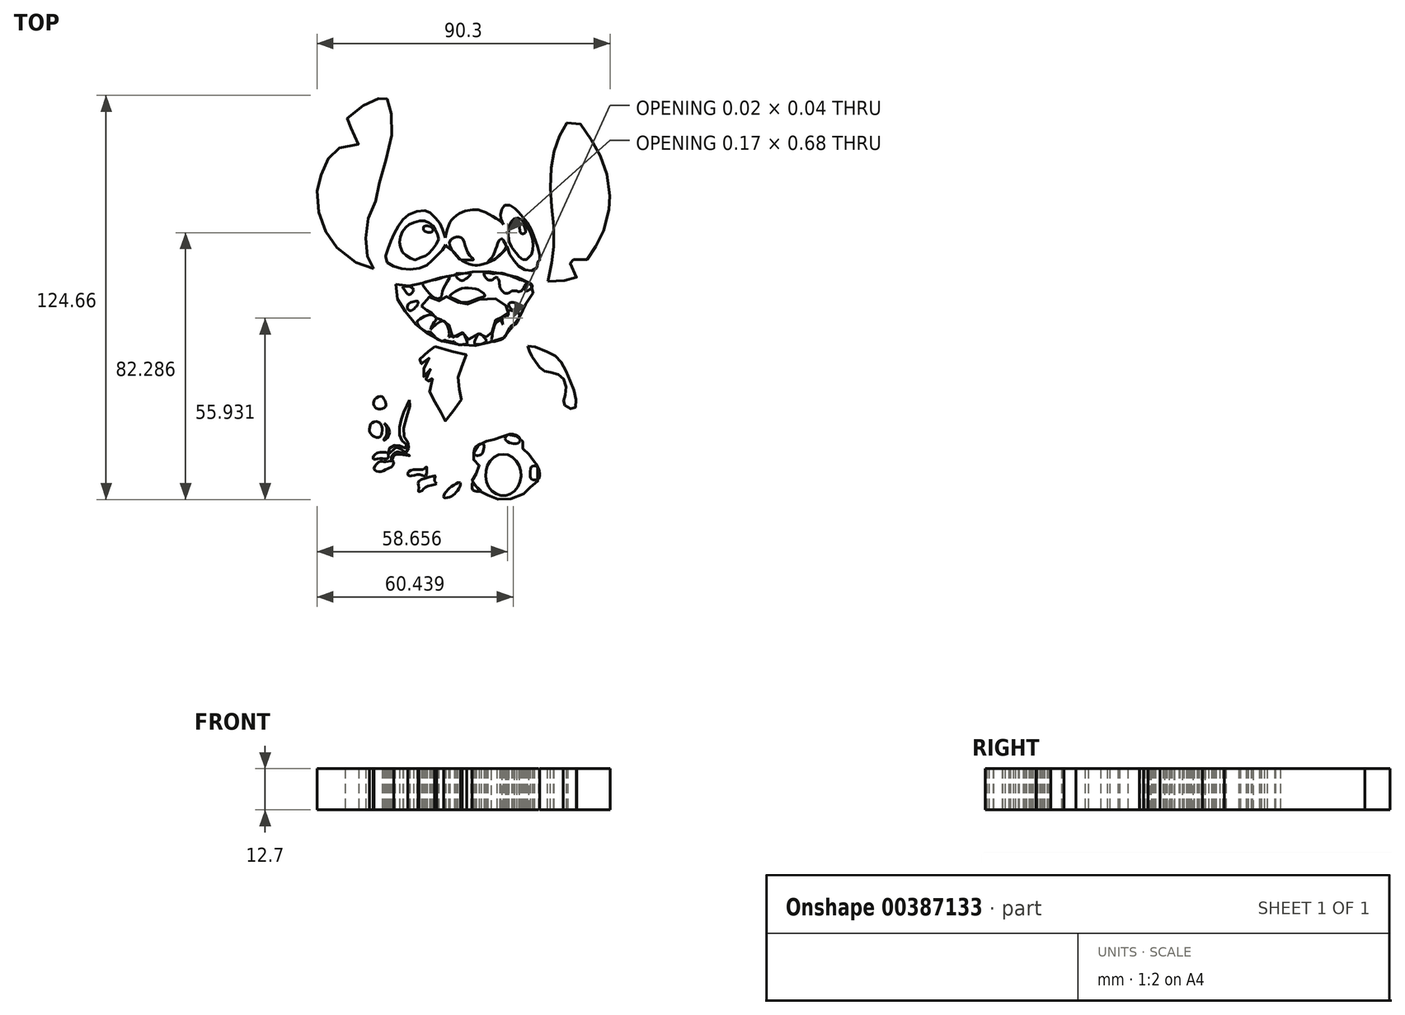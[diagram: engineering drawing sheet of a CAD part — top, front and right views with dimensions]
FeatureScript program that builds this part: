
annotation { "Feature Type Name" : "Feature", "Feature Type Description" : "" }
export const myFeature = defineFeature(function(context is Context, id is Id, definition is map)
    precondition{}
    {
        {
            var Q0;
            Q0=qCreatedBy(makeId("Top.planeOp"),FACE);
            var sketch = newSketch(context, id + "F0", { "sketchPlane" : qUnion([Q0])});
            skFitSpline(sketch, "E0", {"points": [v(-32.55, -2.75) * mm, v(-34, 0) * mm, v(-34.97, 5.48) * mm, v(-34.24, 12.5) * mm, v(-31.82, 18.3) * mm, v(-30.61, 24.6) * mm, v(-27.47, 35.25) * mm, v(-26.98, 44.45) * mm, v(-28.2, 49.04) * mm, v(-29.16, 50.74) * mm, v(-32.3, 49.04) * mm, v(-37.15, 46.87) * mm, v(-41.26, 42.27) * mm, v(-39.32, 40.57) * mm, v(-37.39, 35.5) * mm, v(-44.4, 34.28) * mm, v(-46.83, 30.4) * mm, v(-49, 25.57) * mm, v(-49.97, 20.49) * mm, v(-48.76, 12.02) * mm, v(-45.62, 5.97) * mm, v(-39.32, 0) * mm, v(-32.55, -2.75) * mm]});
            skFitSpline(sketch, "E1", {"points": [v(21.18, -6.62) * mm, v(22.63, 0) * mm, v(22.87, 4.51) * mm, v(22.87, 12.74) * mm, v(21.9, 18.8) * mm, v(22.15, 26.54) * mm, v(22.63, 32.35) * mm, v(24.33, 36.94) * mm, v(25.78, 41.06) * mm, v(29.4, 43) * mm, v(33.04, 39.36) * mm, v(36.43, 33.8) * mm, v(39.09, 27.5) * mm, v(40.3, 19.28) * mm, v(40.06, 16.13) * mm, v(37.88, 7.9) * mm, v(35.46, 3.55) * mm, v(33.04, 0) * mm, v(29.65, 0) * mm, v(27.23, 0) * mm, v(29.4, -2.75) * mm, v(29.65, -5.9) * mm, v(26.26, -6.38) * mm, v(21.18, -6.62) * mm]});
            skFitSpline(sketch, "E2", {"points": [v(-10.38, 4.73) * mm, v(-11.39, 9.62) * mm, v(-12.54, 11.78) * mm, v(-14.99, 14.51) * mm, v(-17.14, 15.23) * mm, v(-21.75, 13.94) * mm, v(-24.34, 11.35) * mm, v(-26.5, 7.46) * mm, v(-28.08, 3.43) * mm, v(-28.8, 0) * mm, v(-26.5, -1.9) * mm, v(-21.9, -2.9) * mm, v(-17.14, -2.18) * mm, v(-14.27, 0) * mm, v(-11.82, 2.57) * mm, v(-10.38, 4.73) * mm]});
            skFitSpline(sketch, "E3", {"points": [v(8.61, 4.15) * mm, v(10.49, 0) * mm, v(12.93, -2.47) * mm, v(16.24, -3.33) * mm, v(17.97, -1.75) * mm, v(18.26, 0) * mm, v(18.69, 0) * mm, v(18.26, 3.15) * mm, v(17.25, 6.02) * mm, v(16.39, 8.61) * mm, v(14.51, 11.92) * mm, v(12.36, 14.37) * mm, v(10.92, 15.95) * mm, v(8.9, 16.96) * mm, v(7.32, 16.39) * mm, v(6.6, 14.37) * mm, v(6.6, 13.22) * mm, v(7.46, 10.92) * mm, v(8.76, 8.04) * mm, v(8.61, 4.15) * mm]});
            skFitSpline(sketch, "E4", {"points": [v(0, 15.38) * mm, v(-2.6, 15.38) * mm, v(-4.77, 14.95) * mm, v(-7.93, 12.93) * mm, v(-9.66, 10.05) * mm, v(-10.38, 4.73) * mm, v(-8.08, 2.71) * mm, v(-5.63, 0) * mm, v(-1.75, -1.6) * mm, v(0, -1.6) * mm, v(4.44, 0) * mm, v(6.89, 2) * mm, v(8.61, 4.15) * mm, v(8.76, 8.04) * mm, v(7.46, 10.92) * mm, v(4.59, 13.22) * mm, v(0, 15.38) * mm]});
            skFitSpline(sketch, "E5", {"points": [v(-25.63, -7.5) * mm, v(-23.04, -7.8) * mm, v(-19.45, -7.8) * mm, v(-15.56, -6.5) * mm, v(-9.09, -4.91) * mm, v(-5.78, -4.34) * mm, v(0, -3.47) * mm, v(3.58, -3.62) * mm, v(6.6, -4.2) * mm, v(11.35, -5.2) * mm, v(15.1, -6.64) * mm, v(16.96, -8.8) * mm, v(16.53, -10.24) * mm, v(14.66, -12.97) * mm, v(13.08, -15.85) * mm, v(11.92, -18.73) * mm, v(9.9, -21.03) * mm, v(7.46, -24.05) * mm, v(3.87, -25.2) * mm, v(0, -26.35) * mm, v(-4.34, -26.21) * mm, v(-10.38, -25.5) * mm, v(-14.27, -23.48) * mm, v(-17.86, -21.6) * mm, v(-20.6, -18.58) * mm, v(-23.76, -14.7) * mm, v(-25.35, -11.53) * mm, v(-25.63, -7.5) * mm]});
            skSolve(sketch);
        }
        {
            var Q0;
            Q0=qCreatedBy(makeId("Top.planeOp"),FACE);
            var sketch = newSketch(context, id + "F1", { "sketchPlane" : qUnion([Q0])});
            skFitSpline(sketch, "E6", {"points": [v(-9.14, 5.43) * mm, v(-7.56, 7.02) * mm, v(-6.12, 7.02) * mm, v(-4.97, 6.3) * mm, v(-4.25, 4.14) * mm, v(-2.95, 1.4) * mm, v(-1.8, 0) * mm, v(-3.39, 0) * mm, v(-5.55, 0) * mm, v(-7.85, 2.27) * mm, v(-9.14, 5.43) * mm]});
            skFitSpline(sketch, "E7", {"points": [v(2.63, -0.7) * mm, v(3.84, 0.7) * mm, v(4.38, 1.6) * mm, v(4.74, 2.5) * mm, v(5.4, 4.14) * mm, v(6.2, 6.02) * mm, v(7.04, 6.5) * mm, v(7.4, 6.14) * mm, v(8, 4.99) * mm, v(8.31, 4.14) * mm, v(6.92, 2.2) * mm, v(5.35, 0.63) * mm, v(4.5, 0) * mm, v(2.63, -0.7) * mm]});
            skPoint(sketch, "E8.0.internal.orphan", {"position": v(-13.04, 5.43) * mm});
            skPoint(sketch, "E8.1.internal.orphan", {"position": v(-13.73, 4.14) * mm});
            skPoint(sketch, "E8.2.internal.orphan", {"position": v(-15.27, 2.27) * mm});
            skPoint(sketch, "E8.4.internal.orphan", {"position": v(-19.03, 0) * mm});
            skFitSpline(sketch, "E9", {"points": [v(-12.45, 6.44) * mm, v(-12.96, 8.15) * mm, v(-13.73, 9.7) * mm, v(-14.67, 10.9) * mm, v(-16.21, 11.83) * mm, v(-17.75, 12.09) * mm, v(-20.23, 11.49) * mm, v(-21.86, 10.72) * mm, v(-23.06, 9.6) * mm, v(-24.17, 7.81) * mm, v(-24.51, 5.5) * mm, v(-24.25, 4.13) * mm, v(-23.31, 2) * mm, v(-21.86, 1.05) * mm, v(-20.15, 0) * mm, v(-18.18, 0.7) * mm, v(-16.3, 1.4) * mm, v(-15.27, 2.27) * mm, v(-13.73, 4.14) * mm, v(-12.45, 6.44) * mm]});
            skFitSpline(sketch, "E10", {"points": [v(9.12, 9.35) * mm, v(9.54, 11.23) * mm, v(10.49, 12.52) * mm, v(11.77, 12.94) * mm, v(13.05, 12.35) * mm, v(14.08, 11.23) * mm, v(15.36, 9.35) * mm, v(16.05, 7.72) * mm, v(16.56, 4.14) * mm, v(16.05, 1.56) * mm, v(15.28, 0.8) * mm, v(14.34, 0) * mm, v(12.54, 0.7) * mm, v(11.26, 2.27) * mm, v(10.49, 3.19) * mm, v(9.29, 5.43) * mm, v(9.12, 9.35) * mm]});
            skFitSpline(sketch, "E11", {"points": [v(14.93, -26.52) * mm, v(15.44, -28.06) * mm, v(16.47, -30.11) * mm, v(18, -32.33) * mm, v(19.9, -34.22) * mm, v(22.11, -34.73) * mm, v(25.37, -35.93) * mm, v(26.74, -39.18) * mm, v(26.22, -42.77) * mm, v(25.88, -44.14) * mm, v(27.6, -45.68) * mm, v(29.47, -45.68) * mm, v(29.64, -42.09) * mm, v(27.76, -36.61) * mm, v(24.85, -30.97) * mm, v(20.75, -28.23) * mm, v(14.93, -26.52) * mm]});
            skFitSpline(sketch, "E12", {"points": [v(-13.65, -26.69) * mm, v(-14.16, -27.37) * mm, v(-16.73, -28.74) * mm, v(-18.44, -30.97) * mm, v(-18.61, -32.5) * mm, v(-15.36, -29.94) * mm, v(-16.22, -31.65) * mm, v(-17.07, -33.7) * mm, v(-17.07, -35.42) * mm, v(-17.07, -36.27) * mm, v(-16.05, -34.9) * mm, v(-14.5, -33.02) * mm, v(-16.22, -35.59) * mm, v(-16.39, -37.3) * mm, v(-16.39, -38.32) * mm, v(-14.34, -35.59) * mm, v(-15.02, -38.67) * mm, v(-15.2, -41.23) * mm, v(-13.3, -44.31) * mm, v(-11.6, -47.4) * mm, v(-10.74, -49.62) * mm, v(-9.89, -49.1) * mm, v(-6.8, -44.83) * mm, v(-5.27, -42.09) * mm, v(-6.46, -39.18) * mm, v(-6.46, -36.1) * mm, v(-5.78, -33.7) * mm, v(-3.9, -29.43) * mm, v(-6.12, -28.91) * mm, v(-13.65, -26.69) * mm]});
            skEllipse(sketch, "E13", {"center": v(7.4, -66.32) * mm, "majorRadius": 6.41 * mm, "minorRadius": 5.47 * mm, "majorAxis": v(0, 1)});
            skFitSpline(sketch, "E14", {"points": [v(-29.26, -50.47) * mm, v(-28.65, -51.43) * mm, v(-28.53, -52.52) * mm, v(-28.53, -53.85) * mm, v(-29.14, -54.94) * mm, v(-29.38, -55.67) * mm, v(-28.05, -54.46) * mm, v(-27.68, -52.76) * mm, v(-28.29, -51.31) * mm, v(-29.26, -50.47) * mm]});
            skFitSpline(sketch, "E15", {"points": [v(-31.68, -49.86) * mm, v(-33.25, -50.47) * mm, v(-33.61, -51.07) * mm, v(-33.86, -52.64) * mm, v(-33.25, -53.85) * mm, v(-32.28, -54.58) * mm, v(-30.7, -54.7) * mm, v(-29.98, -53.37) * mm, v(-29.98, -51.55) * mm, v(-30.47, -50.47) * mm, v(-31.68, -49.86) * mm]});
            skFitSpline(sketch, "E16", {"points": [v(-32.16, -42.96) * mm, v(-32.52, -44.54) * mm, v(-32.04, -45.5) * mm, v(-31.44, -45.87) * mm, v(-29.86, -45.87) * mm, v(-28.77, -45.02) * mm, v(-28.77, -44.17) * mm, v(-29.5, -42.6) * mm, v(-30.23, -42.12) * mm, v(-32.16, -42.96) * mm]});
            skFitSpline(sketch, "E17", {"points": [v(-1.3, -60.15) * mm, v(-1.55, -58.81) * mm, v(-1.18, -57.73) * mm, v(0, -56.88) * mm, v(1.24, -56.76) * mm, v(1.48, -57.73) * mm, v(1, -59.54) * mm, v(0, -60.27) * mm, v(-1.3, -60.15) * mm]});
            skFitSpline(sketch, "E18", {"points": [v(8.01, -55.18) * mm, v(8.98, -53.85) * mm, v(10.2, -53.73) * mm, v(11.52, -54.1) * mm, v(12.5, -54.94) * mm, v(12.25, -56.27) * mm, v(11.16, -56.64) * mm, v(9.7, -56.52) * mm, v(8.01, -55.18) * mm]});
            skFitSpline(sketch, "E19", {"points": [v(16, -63.9) * mm, v(17.09, -63.53) * mm, v(18.06, -63.9) * mm, v(18.54, -65.47) * mm, v(18.42, -67.29) * mm, v(17.57, -67.77) * mm, v(16.36, -67.77) * mm, v(15.76, -67.04) * mm, v(15.76, -65.95) * mm, v(16, -63.9) * mm]});
            skFitSpline(sketch, "E20", {"points": [v(-9.14, -11.19) * mm, v(-7.77, -11.95) * mm, v(-6.19, -12.77) * mm, v(-5.07, -13.12) * mm, v(-4.2, -13.12) * mm, v(-2.58, -12.77) * mm, v(0, -11.75) * mm, v(1.8, -11.09) * mm, v(1.29, -10.32) * mm, v(0, -9.3) * mm, v(-1.1, -8.95) * mm, v(-2.93, -8.65) * mm, v(-4.51, -8.65) * mm, v(-5.94, -9) * mm, v(-7.56, -9.87) * mm, v(-9.14, -11.19) * mm]});
            skFitSpline(sketch, "E21", {"points": [v(-17.79, -14.2) * mm, v(-16.87, -12.72) * mm, v(-15.4, -11.44) * mm, v(-14.23, -11.95) * mm, v(-12.65, -12.51) * mm, v(-11.33, -12.51) * mm, v(-10.62, -11.24) * mm, v(-9.5, -11.65) * mm, v(-7.3, -12.61) * mm, v(-5.48, -13.78) * mm, v(-4.71, -13.94) * mm, v(-3.04, -13.48) * mm, v(-0.95, -12.77) * mm, v(0.88, -11.95) * mm, v(4.95, -11.95) * mm, v(6.68, -12.77) * mm, v(8.41, -14.24) * mm, v(9.02, -15) * mm, v(8.77, -15.72) * mm, v(9.07, -16.79) * mm, v(8.31, -16.94) * mm, v(7.65, -17.14) * mm, v(6.78, -18.06) * mm, v(6.12, -18.41) * mm, v(5.3, -18.41) * mm, v(4.55, -19.18) * mm, v(4.04, -21.57) * mm, v(3.22, -23.9) * mm, v(2.46, -24.16) * mm, v(1.95, -23.45) * mm, v(0.63, -22.38) * mm, v(0, -22.48) * mm, v(-1.3, -24.47) * mm, v(-3.24, -24.57) * mm, v(-3.7, -23.55) * mm, v(-4.51, -22.59) * mm, v(-5.83, -22.64) * mm, v(-7.36, -24.01) * mm, v(-8.63, -23.4) * mm, v(-9.04, -21.57) * mm, v(-9.85, -18.67) * mm, v(-10.62, -18.36) * mm, v(-12.5, -18.72) * mm, v(-13.26, -19.13) * mm, v(-13.31, -18.26) * mm, v(-13.26, -17.1) * mm, v(-13.57, -16.48) * mm, v(-14.79, -16.48) * mm, v(-16.47, -16.94) * mm, v(-16.21, -15.72) * mm, v(-16.16, -14.6) * mm, v(-17.23, -14.24) * mm, v(-17.79, -14.2) * mm]});
            skFitSpline(sketch, "E22", {"points": [v(0.6, -71.32) * mm, v(0, -71.41) * mm, v(-1.88, -71.07) * mm, v(-2.22, -70.21) * mm, v(-2.22, -69.19) * mm, v(-2.05, -68.76) * mm, v(-1.28, -69.53) * mm, v(0.6, -71.32) * mm]});
            skFitSpline(sketch, "E23", {"points": [v(-5.9, -68.67) * mm, v(-6.24, -70.47) * mm, v(-7.61, -72.18) * mm, v(-9.24, -73.2) * mm, v(-10.78, -73.3) * mm, v(-10.95, -72.78) * mm, v(-10, -71.24) * mm, v(-8.12, -69.61) * mm, v(-5.9, -68.67) * mm]});
            skFitSpline(sketch, "E24", {"points": [v(-13.17, -69.01) * mm, v(-16, -69.78) * mm, v(-17.62, -71.07) * mm, v(-18.65, -71.5) * mm, v(-18.65, -70.13) * mm, v(-18.73, -68.33) * mm, v(-14.54, -66.79) * mm, v(-13.52, -66.62) * mm, v(-13.77, -68.24) * mm, v(-13.17, -69.01) * mm]});
            skFitSpline(sketch, "E25", {"points": [v(-16.5, -66.53) * mm, v(-18.56, -66.2) * mm, v(-21.64, -66.62) * mm, v(-21.73, -65.34) * mm, v(-18.4, -64.65) * mm, v(-16.94, -64.48) * mm, v(-16.25, -63.8) * mm, v(-16.5, -66.53) * mm]});
            skFitSpline(sketch, "E26", {"points": [v(-26.7, -63.54) * mm, v(-28.4, -64.48) * mm, v(-30.8, -65.34) * mm, v(-32.43, -64.3) * mm, v(-30.37, -62.08) * mm, v(-29, -62.25) * mm, v(-26.52, -62.08) * mm, v(-26.7, -63.54) * mm]});
            skFitSpline(sketch, "E27", {"points": [v(-32.68, -60.89) * mm, v(-32.6, -61.4) * mm, v(-30.37, -61.23) * mm, v(-28.23, -61.23) * mm, v(-28.06, -59.77) * mm, v(-29, -59.35) * mm, v(-30.97, -59.43) * mm, v(-32.17, -60.03) * mm, v(-32.68, -60.89) * mm]});
            skSolve(sketch);
        }
        {
            var Q0;
            Q0 = qSketchRegion(id + "F1", true);
            extrude(context, id + "F2", {"entities" : qUnion([Q0]), "depth" : 12.7 * mm});
        }
        {
            var Q0;
            Q0 = qSketchRegion(id + "F0", true);
            extrude(context, id + "F3", {"entities" : qUnion([Q0]), "depth" : 12.7 * mm});
        }
        {
            var Q0;
            Q0=qCreatedBy(makeId("Top.planeOp"),FACE);
            var sketch = newSketch(context, id + "F4", { "sketchPlane" : qUnion([Q0])});
            skFitSpline(sketch, "E28", {"points": [v(-23.55, -8.28) * mm, v(-22.83, -9.5) * mm, v(-21.62, -10.7) * mm, v(-20.29, -9.5) * mm, v(-21.01, -8.4) * mm, v(-23.55, -8.28) * mm]});
            skFitSpline(sketch, "E29", {"points": [v(-21.86, -13.6) * mm, v(-20.17, -12.88) * mm, v(-18.83, -12.88) * mm, v(-19.08, -13.97) * mm, v(-19.56, -14.57) * mm, v(-21.13, -15.66) * mm, v(-22.1, -14.94) * mm, v(-21.86, -13.6) * mm]});
            skFitSpline(sketch, "E30", {"points": [v(-17.38, -7.2) * mm, v(-16.78, -8.64) * mm, v(-15.45, -10.34) * mm, v(-13.51, -11.8) * mm, v(-11.94, -11.67) * mm, v(-11.57, -10.82) * mm, v(-11.21, -9.37) * mm, v(-10.12, -7.07) * mm, v(-9.15, -5.13) * mm, v(-10.6, -5.26) * mm, v(-13.39, -6.1) * mm, v(-17.38, -7.2) * mm]});
            skFitSpline(sketch, "E31", {"points": [v(-7.34, -4.4) * mm, v(-6.13, -6.1) * mm, v(-4.56, -6.1) * mm, v(-2.62, -4.29) * mm, v(-4.92, -4.17) * mm, v(-7.34, -4.4) * mm]});
            skFitSpline(sketch, "E32", {"points": [v(8.15, -10.34) * mm, v(9.97, -9.5) * mm, v(11.54, -7.2) * mm, v(12.14, -6.1) * mm, v(10.09, -5.13) * mm, v(6.33, -4.17) * mm, v(5.37, -5.13) * mm, v(5.97, -6.1) * mm, v(6.46, -8.52) * mm, v(8.15, -10.34) * mm]});
            skFitSpline(sketch, "E33", {"points": [v(2.7, -6.1) * mm, v(4.04, -6.1) * mm, v(5.37, -5.13) * mm, v(6.33, -4.17) * mm, v(4.16, -4.17) * mm, v(1.5, -4.17) * mm, v(2.7, -6.1) * mm]});
            skFitSpline(sketch, "E34", {"points": [v(-15.69, -22.32) * mm, v(-14.96, -21.47) * mm, v(-14.48, -20.02) * mm, v(-13.27, -18.2) * mm, v(-14.36, -17) * mm, v(-16.66, -17.36) * mm, v(-18.71, -18.57) * mm, v(-19.2, -19.53) * mm, v(-15.69, -22.32) * mm]});
            skFitSpline(sketch, "E35", {"points": [v(-15.12, -21.94) * mm, v(-14.12, -23.16) * mm, v(-13.39, -24.01) * mm, v(-11.7, -24.98) * mm, v(-10.49, -24.74) * mm, v(-9.4, -23.77) * mm, v(-9.4, -21.47) * mm, v(-9.88, -20.26) * mm, v(-10.73, -18.93) * mm, v(-11.82, -18.93) * mm, v(-13.27, -19.9) * mm, v(-15.12, -21.94) * mm]});
            skFitSpline(sketch, "E36", {"points": [v(-7.7, -25.1) * mm, v(-6.85, -23.77) * mm, v(-5.04, -22.8) * mm, v(-4.31, -23.77) * mm, v(-3.83, -25.1) * mm, v(-3.83, -25.83) * mm, v(-4.92, -26.07) * mm, v(-6.5, -26.07) * mm, v(-7.7, -25.1) * mm]});
            skFitSpline(sketch, "E37", {"points": [v(-1.05, -26.07) * mm, v(-1.4, -25.1) * mm, v(0, -22.8) * mm, v(1.37, -23.77) * mm, v(2.1, -25.1) * mm, v(-1.05, -26.07) * mm]});
            skFitSpline(sketch, "E38", {"points": [v(4.04, -25.1) * mm, v(3.91, -23.77) * mm, v(4.28, -21.47) * mm, v(4.88, -20.02) * mm, v(6.33, -18.57) * mm, v(7.3, -20.02) * mm, v(8.15, -21.47) * mm, v(8.15, -22.44) * mm, v(7.9, -23.77) * mm, v(4.04, -25.1) * mm]});
            skFitSpline(sketch, "E39", {"points": [v(7.3, -20.02) * mm, v(7.3, -17.84) * mm, v(9.12, -17.11) * mm, v(10.45, -17.96) * mm, v(10.93, -20.02) * mm, v(10.33, -20.02) * mm, v(7.9, -23.77) * mm], "startDerivative": vector(-3.13, 14.17) * mm, "endDerivative": vector(-10.3, -21.64) * mm});
            skFitSpline(sketch, "E40", {"points": [v(9.12, -17.11) * mm, v(9.12, -15.66) * mm, v(10.45, -15.66) * mm, v(11.42, -15.66) * mm, v(12.39, -17.11) * mm, v(10.93, -20.02) * mm, v(10.45, -17.96) * mm, v(9.12, -17.11) * mm]});
            skFitSpline(sketch, "E41", {"points": [v(10.93, -15.64) * mm, v(9.12, -13.6) * mm, v(11.42, -13.6) * mm, v(10.93, -15.64) * mm]});
            skFitSpline(sketch, "E42", {"points": [v(9.97, -9.5) * mm, v(11.54, -9.5) * mm], "startDerivative": vector(1.57, 0) * mm, "endDerivative": vector(1.57, 0) * mm});
            skFitSpline(sketch, "E43", {"points": [v(15.29, -7.2) * mm, v(14.68, -7.2) * mm, v(13, -9.5) * mm, v(11.54, -9.5) * mm, v(11.54, -7.2) * mm, v(12.14, -6.1) * mm, v(15.29, -7.2) * mm]});
            skFitSpline(sketch, "E44", {"points": [v(15.41, -7.31) * mm, v(16.38, -8.16) * mm, v(14.8, -9.5) * mm, v(14.2, -9.5) * mm, v(15.41, -7.31) * mm]});
            skFitSpline(sketch, "E45", {"points": [v(-9.4, -25.1) * mm, v(-10.49, -24.74) * mm, v(-9.4, -23.77) * mm, v(-6.85, -23.77) * mm, v(-7.7, -25.1) * mm, v(-9.4, -25.1) * mm]});
            skFitSpline(sketch, "E46", {"points": [v(-16.79, 10.45) * mm, v(-17.22, 9.87) * mm, v(-16.79, 8.86) * mm, v(-14.77, 8.58) * mm, v(-14.34, 9.73) * mm, v(-16.79, 10.45) * mm]});
            skFitSpline(sketch, "E47", {"points": [v(12.42, 9.73) * mm, v(13, 8.14) * mm, v(13.86, 8.14) * mm, v(14.3, 9) * mm, v(13.43, 10.88) * mm, v(12.71, 11.17) * mm, v(12.42, 9.73) * mm]});
            skFitSpline(sketch, "E48", {"points": [v(-26.93, -61.89) * mm, v(-26.32, -60.46) * mm, v(-23.88, -60.05) * mm, v(-21.44, -60.36) * mm, v(-23.88, -59.44) * mm, v(-25.3, -59.24) * mm, v(-26.93, -60.46) * mm, v(-26.93, -61.89) * mm]});
            skFitSpline(sketch, "E49", {"points": [v(-21.54, -43.16) * mm, v(-22.25, -44.69) * mm, v(-23.37, -47.34) * mm, v(-24.28, -49.98) * mm, v(-24.6, -52.83) * mm, v(-24.18, -55.27) * mm, v(-22.96, -56.5) * mm, v(-22.25, -57.3) * mm, v(-22.66, -58.02) * mm, v(-24.49, -57.4) * mm, v(-25.6, -57.1) * mm, v(-26.93, -57.51) * mm, v(-28.15, -58.94) * mm, v(-27.95, -60.26) * mm, v(-26.93, -58.63) * mm, v(-25, -57.82) * mm, v(-23.98, -58.53) * mm, v(-22.56, -59.44) * mm, v(-21.74, -58.12) * mm, v(-21.64, -56.8) * mm, v(-22.96, -54.87) * mm, v(-23.17, -51.1) * mm, v(-21.44, -45.2) * mm, v(-21.54, -43.16) * mm]});
            skFitSpline(sketch, "E50", {"points": [v(18.05, -63.51) * mm, v(17.74, -62.5) * mm, v(16.62, -61.78) * mm, v(15.8, -61.48) * mm, v(15.4, -60.46) * mm, v(14.28, -58.22) * mm, v(13.47, -58.22) * mm, v(13.87, -57.4) * mm, v(13.57, -56.19) * mm, v(12.35, -55.27) * mm, v(11.74, -54.46) * mm, v(10.41, -53.85) * mm, v(9.1, -53.85) * mm, v(8.38, -54.36) * mm, v(7.56, -54.36) * mm, v(6.14, -54.97) * mm, v(5.02, -55.17) * mm, v(3.5, -56.09) * mm, v(2.58, -55.88) * mm, v(1.46, -56.29) * mm, v(0, -57) * mm, v(-1.7, -58.53) * mm, v(-1.7, -59.44) * mm, v(-1.5, -60.46) * mm, v(-1.7, -61.48) * mm, v(-1.29, -62.6) * mm, v(0, -63.31) * mm, v(-0.88, -64.53) * mm, v(-0.98, -66.16) * mm, v(-1.9, -66.97) * mm, v(-2.1, -68.5) * mm, v(0, -71.15) * mm, v(1.76, -71.76) * mm, v(2.78, -72.67) * mm, v(5.02, -73.59) * mm, v(8.28, -73.9) * mm, v(11.23, -73.28) * mm, v(14.28, -71.65) * mm, v(15.3, -70.23) * mm, v(16.82, -70.03) * mm, v(18.05, -68.1) * mm, v(18.05, -63.51) * mm]});
            skSolve(sketch);
        }
        {
            var Q0;
            Q0 = qSketchRegion(id + "F4", true);
            extrude(context, id + "F5", {"entities" : qUnion([Q0]), "depth" : 12.7 * mm});
        }
    });
